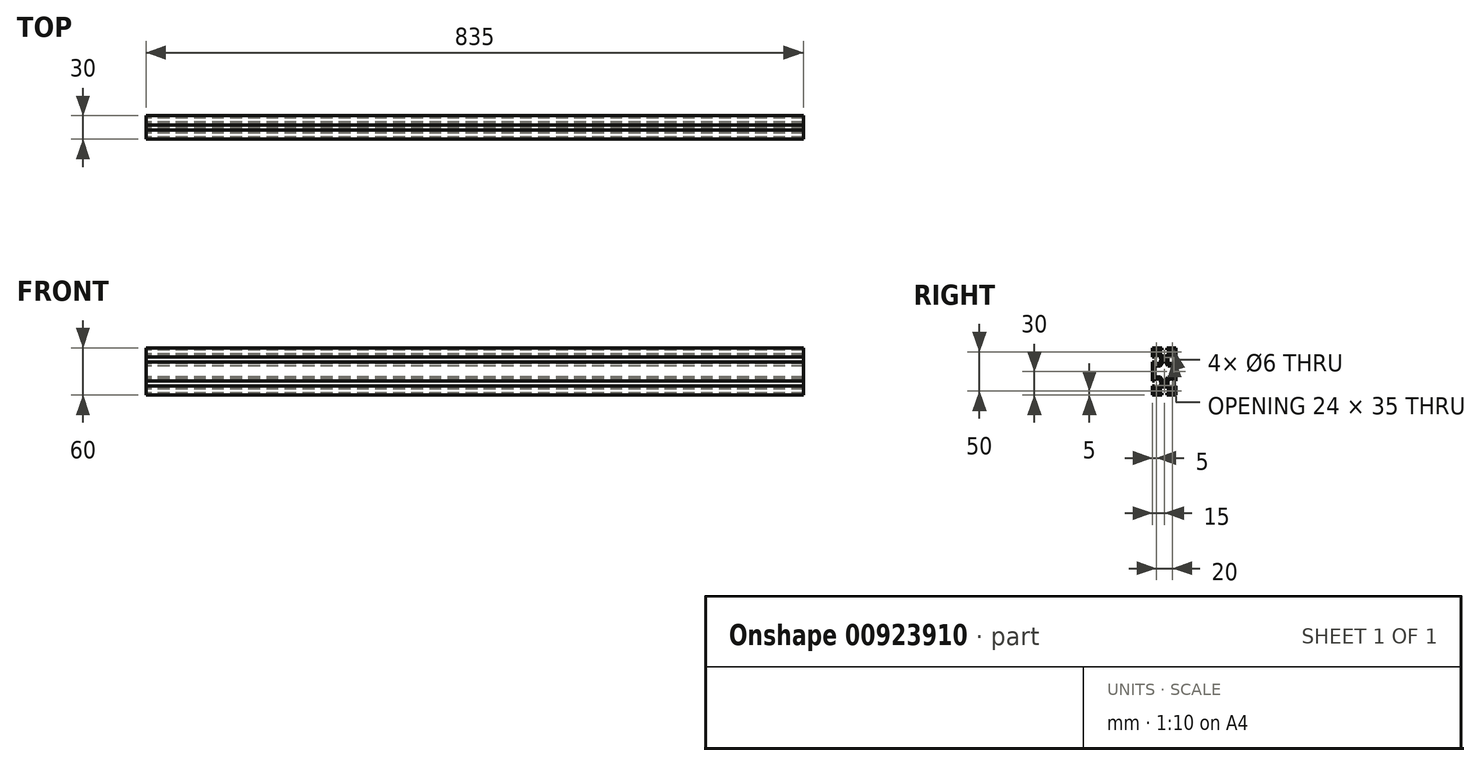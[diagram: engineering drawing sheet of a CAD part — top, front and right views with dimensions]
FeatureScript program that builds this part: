
annotation { "Feature Type Name" : "Feature", "Feature Type Description" : "" }
export const myFeature = defineFeature(function(context is Context, id is Id, definition is map)
    precondition{}
    {
        {
            var Q0;
            Q0=qCreatedBy(makeId("Right.planeOp"),FACE);
            var sketch = newSketch(context, id + "F0", { "sketchPlane" : qUnion([Q0])});
            skArc(sketch, "E0", {"start": v(-9, 6.85) * mm, "mid": v(-11.12, 5.97) * mm, "end": v(-12, 3.85) * mm});
            skLineSegment(sketch, "E1", {"start": v(-9, 6.85) * mm, "end": v(-4.7, 6.85) * mm});
            skLineSegment(sketch, "E2", {"start": v(-4.7, 6.85) * mm, "end": v(-1.25, 12.83) * mm});
            skArc(sketch, "E3", {"start": v(1.25, 12.83) * mm, "mid": v(0, 17.5) * mm, "end": v(-1.25, 12.83) * mm});
            skLineSegment(sketch, "E4", {"start": v(1.25, 12.83) * mm, "end": v(4.7, 6.85) * mm});
            skLineSegment(sketch, "E5", {"start": v(4.7, 6.85) * mm, "end": v(9, 6.85) * mm});
            skArc(sketch, "E6", {"start": v(12, 3.85) * mm, "mid": v(11.12, 5.97) * mm, "end": v(9, 6.85) * mm});
            skLineSegment(sketch, "E7", {"start": v(12, 3.85) * mm, "end": v(12, -3.85) * mm});
            skArc(sketch, "E8", {"start": v(9, -6.85) * mm, "mid": v(11.12, -5.97) * mm, "end": v(12, -3.85) * mm});
            skLineSegment(sketch, "E9", {"start": v(9, -6.85) * mm, "end": v(4.7, -6.85) * mm});
            skLineSegment(sketch, "E10", {"start": v(4.7, -6.85) * mm, "end": v(1.25, -12.83) * mm});
            skArc(sketch, "E11", {"start": v(-1.25, -12.83) * mm, "mid": v(0, -17.5) * mm, "end": v(1.25, -12.83) * mm});
            skLineSegment(sketch, "E12", {"start": v(-1.25, -12.83) * mm, "end": v(-4.7, -6.85) * mm});
            skLineSegment(sketch, "E13", {"start": v(-4.7, -6.85) * mm, "end": v(-9, -6.85) * mm});
            skArc(sketch, "E14", {"start": v(-12, -3.85) * mm, "mid": v(-11.12, -5.97) * mm, "end": v(-9, -6.85) * mm});
            skLineSegment(sketch, "E15", {"start": v(-12, -3.85) * mm, "end": v(-12, 3.85) * mm});
            skCircle(sketch, "E16", {"center": v(-10, 25) * mm, "radius": 3 * mm});
            skCircle(sketch, "E17", {"center": v(10, 25) * mm, "radius": 3 * mm});
            skCircle(sketch, "E18", {"center": v(-10, -25) * mm, "radius": 3 * mm});
            skCircle(sketch, "E19", {"center": v(10, -25) * mm, "radius": 3 * mm});
            skLineSegment(sketch, "E20", {"start": v(15, -11.85) * mm, "end": v(12.5, -11.85) * mm});
            skLineSegment(sketch, "E21", {"start": v(12.5, -11.85) * mm, "end": v(12.5, -9.85) * mm});
            skLineSegment(sketch, "E22", {"start": v(12.5, -9.85) * mm, "end": v(6.55, -9.85) * mm});
            skArc(sketch, "E23", {"start": v(6.55, -9.85) * mm, "mid": v(4.5, -15) * mm, "end": v(6.55, -20.15) * mm});
            skLineSegment(sketch, "E24", {"start": v(6.55, -20.15) * mm, "end": v(12.5, -20.15) * mm});
            skLineSegment(sketch, "E25", {"start": v(12.5, -20.15) * mm, "end": v(12.5, -18.15) * mm});
            skLineSegment(sketch, "E26", {"start": v(12.5, -18.15) * mm, "end": v(15, -18.15) * mm});
            skLineSegment(sketch, "E27", {"start": v(15, -18.15) * mm, "end": v(15, -30) * mm});
            skLineSegment(sketch, "E28", {"start": v(15, -30) * mm, "end": v(3.15, -30) * mm});
            skLineSegment(sketch, "E29", {"start": v(3.15, -30) * mm, "end": v(3.15, -27.5) * mm});
            skLineSegment(sketch, "E30", {"start": v(3.15, -27.5) * mm, "end": v(5.15, -27.5) * mm});
            skLineSegment(sketch, "E31", {"start": v(5.15, -27.5) * mm, "end": v(5.15, -21.55) * mm});
            skArc(sketch, "E32", {"start": v(5.15, -21.55) * mm, "mid": v(0, -19.5) * mm, "end": v(-5.15, -21.55) * mm});
            skLineSegment(sketch, "E33", {"start": v(-5.15, -21.55) * mm, "end": v(-5.15, -27.5) * mm});
            skLineSegment(sketch, "E34", {"start": v(-5.15, -27.5) * mm, "end": v(-3.15, -27.5) * mm});
            skLineSegment(sketch, "E35", {"start": v(-3.15, -27.5) * mm, "end": v(-3.15, -30) * mm});
            skLineSegment(sketch, "E36", {"start": v(-3.15, -30) * mm, "end": v(-15, -30) * mm});
            skLineSegment(sketch, "E37", {"start": v(-15, -30) * mm, "end": v(-15, -18.15) * mm});
            skLineSegment(sketch, "E38", {"start": v(-15, -18.15) * mm, "end": v(-12.5, -18.15) * mm});
            skLineSegment(sketch, "E39", {"start": v(-12.5, -18.15) * mm, "end": v(-12.5, -20.15) * mm});
            skLineSegment(sketch, "E40", {"start": v(-12.5, -20.15) * mm, "end": v(-6.55, -20.15) * mm});
            skArc(sketch, "E41", {"start": v(-6.55, -20.15) * mm, "mid": v(-4.5, -15) * mm, "end": v(-6.55, -9.85) * mm});
            skLineSegment(sketch, "E42", {"start": v(-6.55, -9.85) * mm, "end": v(-12.5, -9.85) * mm});
            skLineSegment(sketch, "E43", {"start": v(-12.5, -9.85) * mm, "end": v(-12.5, -11.85) * mm});
            skLineSegment(sketch, "E44", {"start": v(-12.5, -11.85) * mm, "end": v(-15, -11.85) * mm});
            skLineSegment(sketch, "E45", {"start": v(-15, -11.85) * mm, "end": v(-15, 11.85) * mm});
            skLineSegment(sketch, "E46", {"start": v(-15, 11.85) * mm, "end": v(-12.5, 11.85) * mm});
            skLineSegment(sketch, "E47", {"start": v(-12.5, 11.85) * mm, "end": v(-12.5, 9.85) * mm});
            skLineSegment(sketch, "E48", {"start": v(-12.5, 9.85) * mm, "end": v(-6.55, 9.85) * mm});
            skArc(sketch, "E49", {"start": v(-6.55, 9.85) * mm, "mid": v(-4.5, 15) * mm, "end": v(-6.55, 20.15) * mm});
            skLineSegment(sketch, "E50", {"start": v(-6.55, 20.15) * mm, "end": v(-12.5, 20.15) * mm});
            skLineSegment(sketch, "E51", {"start": v(-12.5, 20.15) * mm, "end": v(-12.5, 18.15) * mm});
            skLineSegment(sketch, "E52", {"start": v(-12.5, 18.15) * mm, "end": v(-15, 18.15) * mm});
            skLineSegment(sketch, "E53", {"start": v(-15, 18.15) * mm, "end": v(-15, 30) * mm});
            skLineSegment(sketch, "E54", {"start": v(-15, 30) * mm, "end": v(-3.15, 30) * mm});
            skLineSegment(sketch, "E55", {"start": v(-3.15, 30) * mm, "end": v(-3.15, 27.5) * mm});
            skLineSegment(sketch, "E56", {"start": v(-3.15, 27.5) * mm, "end": v(-5.15, 27.5) * mm});
            skLineSegment(sketch, "E57", {"start": v(-5.15, 27.5) * mm, "end": v(-5.15, 21.55) * mm});
            skArc(sketch, "E58", {"start": v(-5.15, 21.55) * mm, "mid": v(0, 19.5) * mm, "end": v(5.15, 21.55) * mm});
            skLineSegment(sketch, "E59", {"start": v(5.15, 21.55) * mm, "end": v(5.15, 27.5) * mm});
            skLineSegment(sketch, "E60", {"start": v(5.15, 27.5) * mm, "end": v(3.15, 27.5) * mm});
            skLineSegment(sketch, "E61", {"start": v(3.15, 27.5) * mm, "end": v(3.15, 30) * mm});
            skLineSegment(sketch, "E62", {"start": v(3.15, 30) * mm, "end": v(15, 30) * mm});
            skLineSegment(sketch, "E63", {"start": v(15, 30) * mm, "end": v(15, 18.15) * mm});
            skLineSegment(sketch, "E64", {"start": v(15, 18.15) * mm, "end": v(12.5, 18.15) * mm});
            skLineSegment(sketch, "E65", {"start": v(12.5, 18.15) * mm, "end": v(12.5, 20.15) * mm});
            skLineSegment(sketch, "E66", {"start": v(12.5, 20.15) * mm, "end": v(6.55, 20.15) * mm});
            skArc(sketch, "E67", {"start": v(6.55, 20.15) * mm, "mid": v(4.5, 15) * mm, "end": v(6.55, 9.85) * mm});
            skLineSegment(sketch, "E68", {"start": v(6.55, 9.85) * mm, "end": v(12.5, 9.85) * mm});
            skLineSegment(sketch, "E69", {"start": v(12.5, 9.85) * mm, "end": v(12.5, 11.85) * mm});
            skLineSegment(sketch, "E70", {"start": v(12.5, 11.85) * mm, "end": v(15, 11.85) * mm});
            skLineSegment(sketch, "E71", {"start": v(15, 11.85) * mm, "end": v(15, -11.85) * mm});
            skSolve(sketch);
        }
        {
            var Q0;
            Q0 = qSketchRegion(id + "F0", true);
            extrude(context, id + "F1", {"entities" : qUnion([Q0]), "depth" : 835 * mm, "offsetDistance" : 25 * mm});
        }
    });
